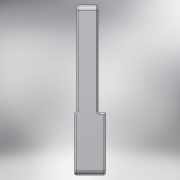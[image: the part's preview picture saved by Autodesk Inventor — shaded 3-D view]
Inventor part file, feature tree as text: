
AUTODESK INVENTOR PART (.ipt)
format: ipt  version: 2018 (Build 220112000, 112)  size: 308,224 bytes
history: native  units: mm
features: extrude x7, fillet x6, other x3, draft x1, chamfer x1
ambient origin geometry x8: Origin, YZ Plane, XZ Plane, XY Plane, X Axis, Y Axis, Z Axis, Center Point
bodies: Solid1 (feature_tree)
feature tree (18):
  other  "Key Sketch"
  extrude  "Upper Key"  Depth=10.0mm
  extrude  "Lower Key"  Depth=1.0mm
  other  "Hinge Cut Sketch"
  extrude  "Hinge Cut"  Depth=10.0mm TaperAngle=0.0deg
  extrude  "Hinge Cut 2"  Depth=3.0mm
  other  "Lever Sketch"
  extrude  "Vertical Lever"  Depth=3.0mm
  extrude  "Horizontal Lever"  Depth=33.6625mm
  extrude  "Spring Hook"  Depth=0.5mm
  draft  "FaceDraft3"
  chamfer  "Chamfer1"  Distance=3.0mm
  fillet  "Fillet9"  Radius=6.0mm
  fillet  "Fillet10"  Radius=4.0mm
  fillet  "Fillet5"  Radius=10.0mm
  fillet  "Fillet4"  [1 undecoded]
  fillet  "Fillet11"  Radius=3.0mm
  fillet  "Fillet14"  Radius=2.3mm
note: 1 required parameter value undecoded (feature->parameter linkage not recoverable at this tier; creation-order binding heuristic only, values carry confidence <= 0.55)
